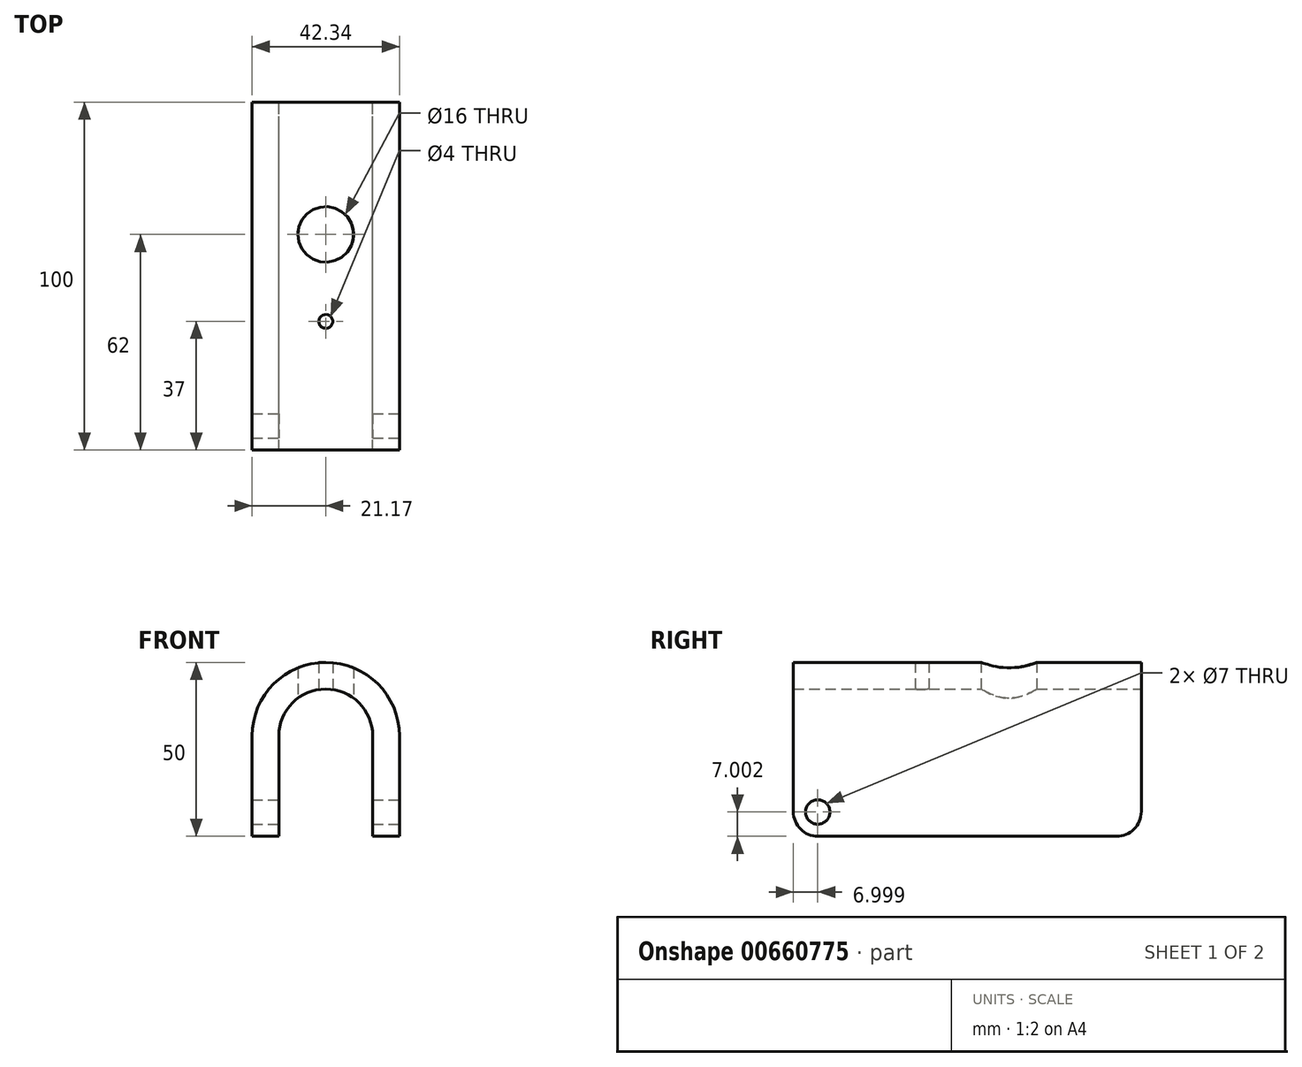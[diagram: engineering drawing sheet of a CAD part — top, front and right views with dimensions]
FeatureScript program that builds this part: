
annotation { "Feature Type Name" : "Feature", "Feature Type Description" : "" }
export const myFeature = defineFeature(function(context is Context, id is Id, definition is map)
    precondition{}
    {
        {
            var Q0;
            Q0=qCreatedBy(makeId("Front.planeOp"),FACE);
            var sketch = newSketch(context, id + "F0", { "sketchPlane" : qUnion([Q0])});
            skArc(sketch, "E0", {"start": v(13.5, 0) * mm, "mid": v(0, 13.5) * mm, "end": v(-13.5, 0) * mm});
            skArc(sketch, "E1", {"start": v(21.17, 0) * mm, "mid": v(0, 21.17) * mm, "end": v(-21.17, 0) * mm});
            skLineSegment(sketch, "E2", {"start": v(-13.5, 0) * mm, "end": v(-13.5, -28.83) * mm});
            skLineSegment(sketch, "E3", {"start": v(-13.5, -28.83) * mm, "end": v(-21.17, -28.83) * mm});
            skLineSegment(sketch, "E4", {"start": v(13.5, 0) * mm, "end": v(13.5, -28.83) * mm});
            skLineSegment(sketch, "E5", {"start": v(13.5, -28.83) * mm, "end": v(21.17, -28.83) * mm});
            skLineSegment(sketch, "E6", {"start": v(21.17, -28.83) * mm, "end": v(21.17, 0) * mm});
            skLineSegment(sketch, "E7", {"start": v(-21.17, 0) * mm, "end": v(-21.17, -28.83) * mm});
            skLineSegment(sketch, "E8", {"start": v(0, 21.17) * mm, "end": v(0, 0) * mm});
            skLineSegment(sketch, "E9", {"start": v(0, 0) * mm, "end": v(0, -28.83) * mm});
            skSolve(sketch);
        }
        {
            var Q0;
            {var subQ0=sQuery(id+"F0.wireOp",EDGE,"E2");Q0=makeQuery(id+"F0.imprint","IMPRINT",FACE,{"disambiguationData":[TD([[makeQuery(id+"F0.imprint","IMPRINT",EDGE,{"derivedFrom":subQ0}),-1.0]])]});}
            var Q1;
            {var subQ0=sQuery(id+"F0.wireOp",EDGE,"E4");Q1=makeQuery(id+"F0.imprint","IMPRINT",FACE,{"disambiguationData":[TD([[makeQuery(id+"F0.imprint","IMPRINT",EDGE,{"derivedFrom":subQ0}),1.0]])]});}
            extrude(context, id + "F1", {"entities" : qUnion([Q0, Q1]), "endBound" : BoundingType.SYMMETRIC, "depth" : 100 * mm, "offsetDistance" : 25 * mm});
        }
        {
            var Q0;
            Q0=makeQuery(id+"F1.opExtrude","CAP_EDGE",EDGE,{"disambiguationData":[OSD([sQuery(id+"F0.wireOp",EDGE,"E5")])],"isStart":true});
            var Q1;
            Q1=makeQuery(id+"F1.opExtrude","CAP_EDGE",EDGE,{"disambiguationData":[OSD([sQuery(id+"F0.wireOp",EDGE,"E3")])],"isStart":true});
            var Q2;
            Q2=makeQuery(id+"F1.opExtrude","CAP_EDGE",EDGE,{"disambiguationData":[OSD([sQuery(id+"F0.wireOp",EDGE,"E3")])],"isStart":false});
            var Q3;
            Q3=makeQuery(id+"F1.opExtrude","CAP_EDGE",EDGE,{"disambiguationData":[OSD([sQuery(id+"F0.wireOp",EDGE,"E5")])],"isStart":false});
            fillet(context, id + "F2", {"entities" : qUnion([Q0, Q1, Q2, Q3]), "radius" : 7.1 * mm, "tangentPropagation" : true, "allowEdgeOverflow" : false});
        }
        {
            var Q0;
            Q0=qCreatedBy(makeId("Right.planeOp"),FACE);
            var sketch = newSketch(context, id + "F3", { "sketchPlane" : qUnion([Q0])});
            skCircle(sketch, "E10", {"center": v(-43, -21.83) * mm, "radius": 3.5 * mm});
            skSolve(sketch);
        }
        {
            var Q0;
            Q0=makeQuery(id+"F3.imprint","IMPRINT",FACE,{"disambiguationData":[TD([[makeQuery(id+"F3.imprint","IMPRINT",EDGE,{"derivedFrom":sQuery(id+"F3.wireOp",EDGE,"E10")}),1.0]])]});
            extrude(context, id + "F4", {"entities" : qUnion([Q0]), "operationType" : NewBodyOperationType.REMOVE, "endBound" : BoundingType.SYMMETRIC, "oppositeDirection" : true, "depth" : 50 * mm, "offsetDistance" : 25 * mm});
        }
        {
            var Q0;
            Q0=qCreatedBy(makeId("Top.planeOp"),FACE);
            var sketch = newSketch(context, id + "F5", { "sketchPlane" : qUnion([Q0])});
            skCircle(sketch, "E11", {"center": v(0, -13) * mm, "radius": 2 * mm});
            skCircle(sketch, "E12", {"center": v(0, 12) * mm, "radius": 8 * mm});
            skSolve(sketch);
        }
        {
            var Q0;
            Q0=makeQuery(id+"F5.imprint","IMPRINT",FACE,{"disambiguationData":[TD([[makeQuery(id+"F5.imprint","IMPRINT",EDGE,{"derivedFrom":sQuery(id+"F5.wireOp",EDGE,"E11")}),1.0]])]});
            var Q1;
            Q1=makeQuery(id+"F5.imprint","IMPRINT",FACE,{"disambiguationData":[TD([[makeQuery(id+"F5.imprint","IMPRINT",EDGE,{"derivedFrom":sQuery(id+"F5.wireOp",EDGE,"E12")}),1.0]])]});
            extrude(context, id + "F6", {"entities" : qUnion([Q0, Q1]), "operationType" : NewBodyOperationType.REMOVE, "depth" : 25 * mm, "offsetDistance" : 25 * mm});
        }
    });
